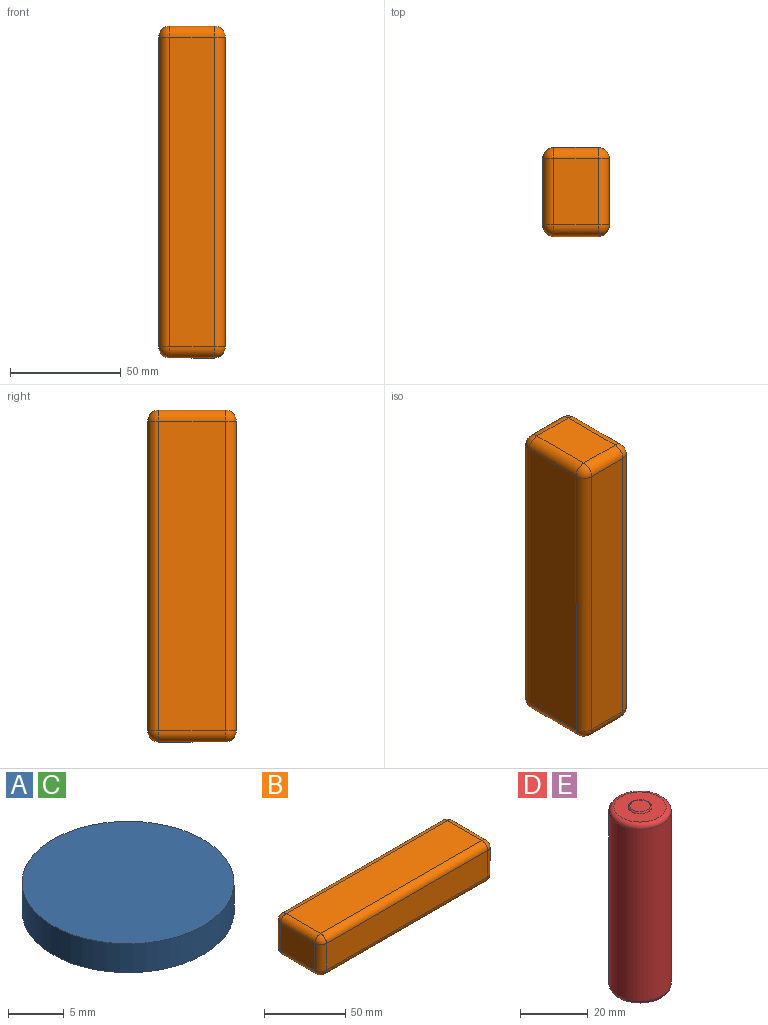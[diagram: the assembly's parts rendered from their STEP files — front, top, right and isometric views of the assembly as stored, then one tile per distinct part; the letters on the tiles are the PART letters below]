
ASSEMBLY  parts=5 mates=4
PART A: 3 faces, bbox 19.1x19.1x3.2 mm
  f0: cylinder r=9.53mm len=19.05mm, axis (0,0,-1), area 190mm2, adj f1,f2
  f1: plane 19.05x19.05mm, normal (0,0,1), area 285mm2, adj f0
  f2: plane 19.05x19.05mm, normal (0,0,-1), area 285mm2, adj f0
PART B: 36 faces, bbox 150x40x30 mm
  f0: plane 140x30mm, normal (0,0,-1), area 3846.6mm2, adj f16,f17,f25,f26,f34,f35
  f1: plane 145x20mm, normal (0,1,0), area 2900mm2, adj f2,f3,f4,f18
  f2: plane 145x30mm, normal (0,0,1), area 3721.7mm2, adj f1,f3,f5,f26,f30,f32
  f3: plane 30x20mm, normal (1,0,0), area 600mm2, adj f1,f2,f4,f5
  f4: plane 145x30mm, normal (0,0,-1), area 4350mm2, adj f1,f3,f5,f23
  f5: plane 145x20mm, normal (0,-1,0), area 2900mm2, adj f2,f3,f4,f29
  f6: plane 30x20mm, normal (-1,0,0), area 600mm2, adj f10,f14,f15,f16
  f7: plane 140x30mm, normal (0,0,1), area 4200mm2, adj f13,f14,f23,f24
  f8: plane 140x20mm, normal (0,-1,0), area 2800mm2, adj f10,f13,f17,f18
  f9: plane 140x20mm, normal (0,1,0), area 2800mm2, adj f15,f24,f25,f29
  f10: cylinder r=5mm len=20mm, axis (0,0,1), area 157.1mm2, adj f6,f8,f11,f12
  f11: sphere r=5mm, area 39.3mm2, adj f10,f13,f14
  f12: sphere r=5mm, area 39.3mm2, adj f10,f16,f17
  f13: cylinder r=5mm len=140mm, axis (1,0,0), area 1099.6mm2, adj f7,f8,f11,f19
  f14: cylinder r=5mm len=30mm, axis (0,-1,0), area 235.6mm2, adj f6,f7,f11,f20
  f15: cylinder r=5mm len=20mm, axis (0,0,1), area 157.1mm2, adj f6,f9,f20,f21
  f16: cylinder r=5mm len=30mm, axis (0,1,0), area 235.6mm2, adj f0,f6,f12,f21
  f17: cylinder r=5mm len=140mm, axis (-1,0,0), area 1099.6mm2, adj f0,f8,f12,f22
  f18: cylinder r=5mm len=20mm, axis (0,0,-1), area 157.1mm2, adj f1,f8,f19,f22
  f19: sphere r=5mm, area 39.3mm2, adj f13,f18,f23
  f20: sphere r=5mm, area 39.3mm2, adj f14,f15,f24
  f21: sphere r=5mm, area 39.3mm2, adj f15,f16,f25
  f22: sphere r=5mm, area 39.3mm2, adj f17,f18,f26
  f23: cylinder r=5mm len=30mm, axis (0,1,0), area 235.6mm2, adj f4,f7,f19,f27
  f24: cylinder r=5mm len=140mm, axis (1,0,0), area 1099.6mm2, adj f7,f9,f20,f27
  f25: cylinder r=5mm len=140mm, axis (-1,0,0), area 1099.6mm2, adj f0,f9,f21,f28
  f26: cylinder r=5mm len=30mm, axis (0,-1,0), area 235.6mm2, adj f0,f2,f22,f28
  f27: sphere r=5mm, area 39.3mm2, adj f23,f24,f29
  f28: sphere r=5mm, area 39.3mm2, adj f25,f26,f29
  f29: cylinder r=5mm len=20mm, axis (0,0,-1), area 157.1mm2, adj f5,f9,f27,f28
  f30: cylinder r=10mm len=20mm, axis (0,0,1), area 188.5mm2, adj f2,f31
  f31: plane 20x20mm, normal (0,0,1), area 137.4mm2, adj f30,f35
  f32: cylinder r=10mm len=20mm, axis (0,0,1), area 188.5mm2, adj f2,f33
  f33: plane 20x20mm, normal (0,0,1), area 137.4mm2, adj f32,f34
  f34: cylinder r=7.5mm len=15mm, axis (0,0,-1), area 94.2mm2, adj f0,f33
  f35: cylinder r=7.5mm len=15mm, axis (0,0,-1), area 94.2mm2, adj f0,f31
PART C: same geometry as A
PART D: 10 faces, bbox 20x20x66.9 mm
  f0: cylinder r=9.25mm len=62.25mm, axis (0,0,-1), area 3618.1mm2, adj f3,f4
  f1: plane 15.45x15.45mm, normal (0,0,1), area 148.9mm2, adj f3,f6
  f2: plane 15.45x15.45mm, normal (0,0,-1), area 167.9mm2, adj f4,f7
  f3: torus R=7.73mm, axis (0,0,1), area 130.8mm2, adj f0,f1
  f4: torus R=7.73mm, axis (0,0,1), area 130.8mm2, adj f0,f2
  f5: plane 6.02x6.02mm, normal (0,0,1), area 28.4mm2, adj f6
  f6: torus R=3.01mm, axis (0,0,-1), area 14.4mm2, adj f1,f5
  f7: cylinder r=2.5mm len=5mm, axis (0,0,1), area 6.8mm2, adj f2,f9
  f8: plane 3.48x3.48mm, normal (0,0,-1), area 9.5mm2, adj f9
  f9: torus R=1.74mm, axis (0,0,-1), area 16.7mm2, adj f7,f8
PART E: same geometry as D
PLACE A rot(axis=(0.58,-0.58,-0.58),120deg) t=(29.07,34.98,37.98)mm
PLACE B rot(axis=(0.71,0,-0.71),180deg) t=(17.66,19.98,-7.02)mm
PLACE C rot(axis=(0.58,-0.58,-0.58),120deg) t=(29.07,34.98,-62.02)mm
PLACE D t=(17.66,34.98,-36.98)mm
PLACE E rot(axis=(0,0,-1),90deg) t=(17.66,34.98,29.92)mm
MATE fastened E.f0 <-> B.f3  axis (0,0,1) through (17.66,34.98,62.98)mm
MATE fastened A.f0 <-> B.f30  axis (1,0,0) through (30.66,34.98,37.98)mm
MATE fastened E.f0 <-> D.f0  axis (0,0,-1) through (17.66,34.98,-3.92)mm
MATE fastened C.f0 <-> B.f32  axis (1,0,0) through (30.66,34.98,-62.02)mm
